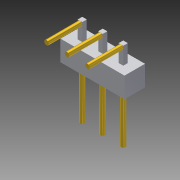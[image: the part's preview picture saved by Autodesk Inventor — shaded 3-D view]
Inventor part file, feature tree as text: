
AUTODESK INVENTOR PART (.ipt)
format: ipt  version: 2014 SP1 (Build 180222100, 222)  size: 104,448 bytes
history: native  units: in
note: dims shown in document units (in); Inventor stores cm internally (conversion verified against a paired STEP export)
features: extrude x1, imported_body x1
ambient origin geometry x8: Origin, YZ Plane, XZ Plane, XY Plane, X Axis, Y Axis, Z Axis, Center Point
bodies: Body1 (feature_tree)
feature tree (2):
  extrude  "Extrude4"  [1 undecoded]
  imported_body  "Base1"
note: 1 required parameter value undecoded (feature->parameter linkage not recoverable at this tier; creation-order binding heuristic only, values carry confidence <= 0.55)
